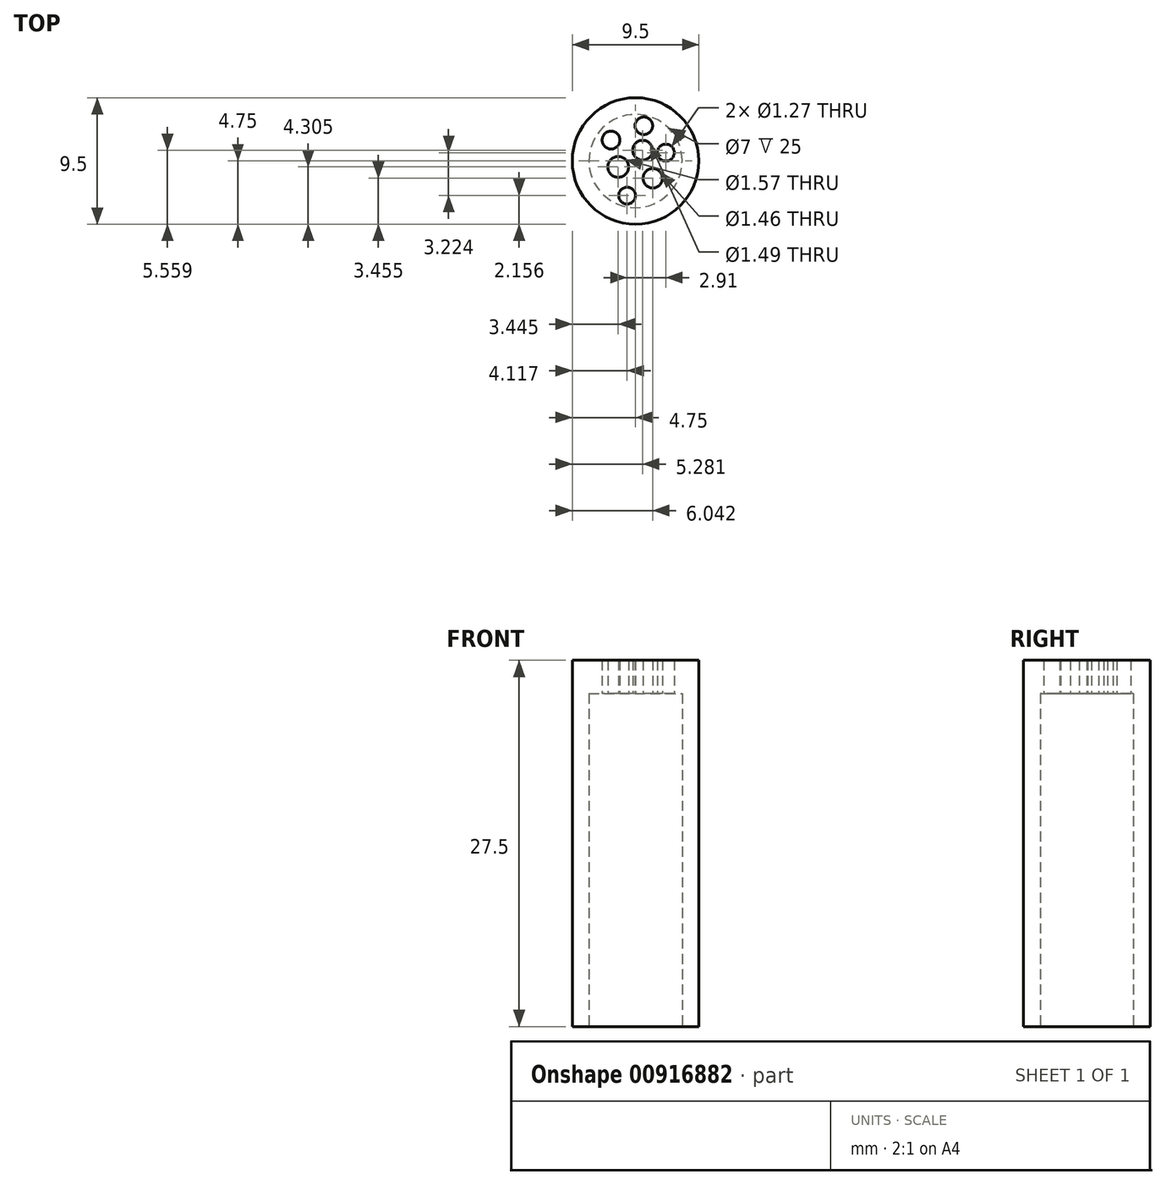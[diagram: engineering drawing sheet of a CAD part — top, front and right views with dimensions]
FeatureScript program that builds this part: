
annotation { "Feature Type Name" : "Feature", "Feature Type Description" : "" }
export const myFeature = defineFeature(function(context is Context, id is Id, definition is map)
    precondition{}
    {
        {
            var Q0;
            Q0=qCreatedBy(makeId("Front.planeOp"),FACE);
            var sketch = newSketch(context, id + "F0", { "sketchPlane" : qUnion([Q0])});
            skLineSegment(sketch, "E0", {"start": v(0, 0) * mm, "end": v(0, 25) * mm});
            skLineSegment(sketch, "E1.bottom", {"start": v(3.5, 0) * mm, "end": v(4.75, 0) * mm});
            skLineSegment(sketch, "E1.top", {"start": v(3.5, 25) * mm, "end": v(4.75, 25) * mm});
            skLineSegment(sketch, "E1.left", {"start": v(3.5, 0) * mm, "end": v(3.5, 25) * mm});
            skLineSegment(sketch, "E1.right", {"start": v(4.75, 0) * mm, "end": v(4.75, 25) * mm});
            skSolve(sketch);
        }
        {
            var Q0;
            Q0 = qSketchRegion(id + "F0", true);
            var Q1;
            Q1=sQuery(id+"F0.wireOp",EDGE,"E0");
            revolve(context, id + "F1", {"surfaceOperationType" : NewSurfaceOperationType.NEW, "entities" : qUnion([Q0]), "axis" : qUnion([Q1]), "revolveType" : RevolveType.FULL});
        }
        {
            var Q0;
            Q0=makeQuery(id+"F1.opRevolve","SWEPT_FACE",FACE,{"disambiguationData":[OSD([sQuery(id+"F0.wireOp",EDGE,"E1.top")])]});
            var sketch = newSketch(context, id + "F2", { "sketchPlane" : qUnion([Q0])});
            skCircle(sketch, "E2", {"center": v(0, 0) * mm, "radius": 4.75 * mm});
            skCircle(sketch, "E3", {"center": v(-1.84, 1.57) * mm, "radius": 0.67 * mm});
            skCircle(sketch, "E4", {"center": v(0.53, 0.8) * mm, "radius": 0.75 * mm});
            skCircle(sketch, "E5", {"center": v(0.62, 2.65) * mm, "radius": 0.66 * mm});
            skCircle(sketch, "E6", {"center": v(-0.63, -2.6) * mm, "radius": 0.63 * mm});
            skCircle(sketch, "E7", {"center": v(1.3, -1.3) * mm, "radius": 0.73 * mm});
            skCircle(sketch, "E8", {"center": v(-1.3, -0.44) * mm, "radius": 0.78 * mm});
            skCircle(sketch, "E9", {"center": v(2.28, 0.63) * mm, "radius": 0.64 * mm});
            skSolve(sketch);
        }
        {
            var Q0;
            Q0 = qSketchRegion(id + "F2", true);
            extrude(context, id + "F3", {"entities" : qUnion([Q0]), "operationType" : NewBodyOperationType.ADD, "depth" : 2.5 * mm, "offsetDistance" : 25 * mm});
        }
    });
